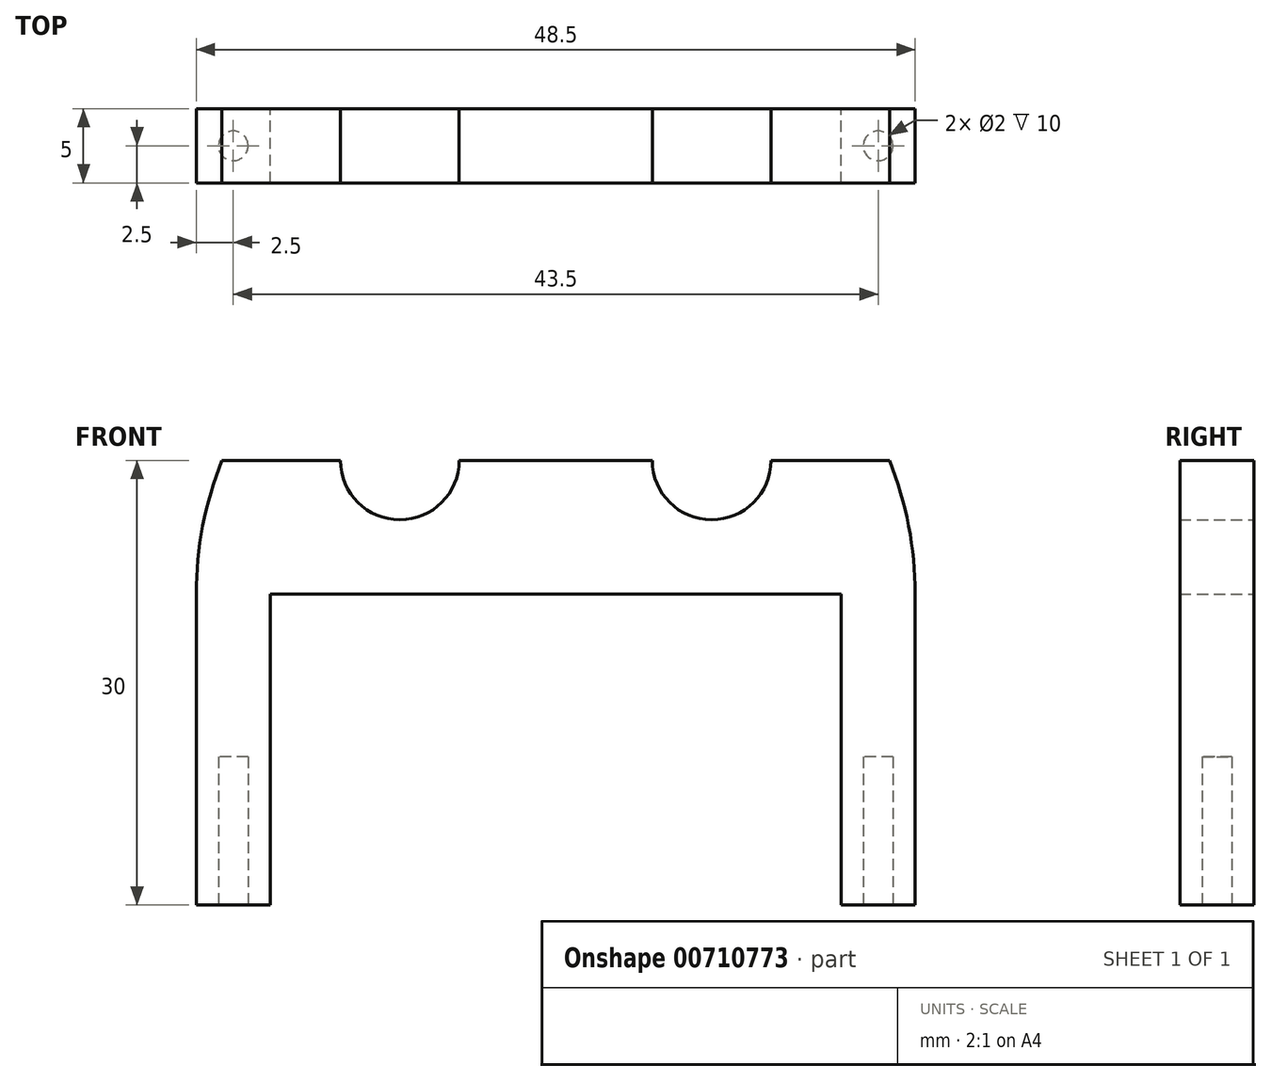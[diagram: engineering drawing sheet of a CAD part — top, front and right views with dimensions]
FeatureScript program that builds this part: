
annotation { "Feature Type Name" : "Feature", "Feature Type Description" : "" }
export const myFeature = defineFeature(function(context is Context, id is Id, definition is map)
    precondition{}
    {
        {
            var Q0;
            Q0=qCreatedBy(makeId("Front.planeOp"),FACE);
            var sketch = newSketch(context, id + "F0", { "sketchPlane" : qUnion([Q0])});
            skLineSegment(sketch, "E0", {"start": v(-24.25, 0) * mm, "end": v(-19.25, 0) * mm});
            skLineSegment(sketch, "E1", {"start": v(19.25, 0) * mm, "end": v(24.25, 0) * mm});
            skLineSegment(sketch, "E2", {"start": v(-24.25, 0) * mm, "end": v(-24.25, 21) * mm});
            skLineSegment(sketch, "E3", {"start": v(-19.25, 0) * mm, "end": v(-19.25, 21) * mm});
            skLineSegment(sketch, "E4", {"start": v(19.25, 0) * mm, "end": v(19.25, 21) * mm});
            skLineSegment(sketch, "E5", {"start": v(24.25, 0) * mm, "end": v(24.25, 21) * mm});
            skArc(sketch, "E6", {"start": v(24.25, 21) * mm, "mid": v(0, 45.25) * mm, "end": v(-24.25, 21) * mm});
            skLineSegment(sketch, "E7", {"start": v(-22.52, 30) * mm, "end": v(22.52, 30) * mm});
            skCircle(sketch, "E8", {"center": v(-10.52, 30) * mm, "radius": 4 * mm});
            skCircle(sketch, "E9", {"center": v(10.52, 30) * mm, "radius": 4 * mm});
            skLineSegment(sketch, "E10", {"start": v(0, 45.25) * mm, "end": v(0, 21) * mm});
            skCircle(sketch, "E11", {"center": v(0, 33.12) * mm, "radius": 1.75 * mm});
            skLineSegment(sketch, "E12", {"start": v(-19.25, 21) * mm, "end": v(19.25, 21) * mm});
            skSolve(sketch);
        }
        {
            var Q0;
            {var subQ1=sQuery(id+"F0.wireOp",EDGE,"E7");var subQ6=sQuery(id+"F0.wireOp",EDGE,"E6");var subQ7=makeQuery(id+"F0.imprint","INTERSECT",VERTEX,{"disambiguationData":[OD(0.0)],"derivedFrom":[subQ6,subQ1]});Q0=makeQuery(id+"F0.imprint","IMPRINT",FACE,{"disambiguationData":[TD([[makeQuery(id+"F0.imprint","IMPRINT",EDGE,{"disambiguationData":[TD([[subQ7,1.0]])],"derivedFrom":subQ6}),1.0]])]});}
            var Q1;
            {var subQ0=sQuery(id+"F0.wireOp",EDGE,"E7");var subQ1=sQuery(id+"F0.wireOp",EDGE,"E6");var subQ2=makeQuery(id+"F0.imprint","INTERSECT",VERTEX,{"disambiguationData":[OD(1.0)],"derivedFrom":[subQ1,subQ0]});Q1=makeQuery(id+"F0.imprint","IMPRINT",FACE,{"disambiguationData":[TD([[makeQuery(id+"F0.imprint","IMPRINT",EDGE,{"disambiguationData":[TD([[subQ2,-1.0]])],"derivedFrom":subQ1}),1.0]])]});}
            var Q2;
            Q2=makeQuery(id+"F0.imprint","IMPRINT",FACE,{"disambiguationData":[TD([[makeQuery(id+"F0.imprint","IMPRINT",EDGE,{"derivedFrom":sQuery(id+"F0.wireOp",EDGE,"E1")}),1.0]])]});
            var Q3;
            Q3=makeQuery(id+"F0.imprint","IMPRINT",FACE,{"disambiguationData":[TD([[makeQuery(id+"F0.imprint","IMPRINT",EDGE,{"derivedFrom":sQuery(id+"F0.wireOp",EDGE,"E0")}),1.0]])]});
            extrude(context, id + "F1", {"entities" : qUnion([Q0, Q1, Q2, Q3]), "depth" : 5 * mm, "offsetDistance" : 25 * mm});
        }
        {
            var Q0;
            Q0=qCreatedBy(makeId("Top.planeOp"),FACE);
            var sketch = newSketch(context, id + "F2", { "sketchPlane" : qUnion([Q0])});
            skCircle(sketch, "E13", {"center": v(-21.75, -2.5) * mm, "radius": 1 * mm});
            skCircle(sketch, "E14", {"center": v(21.75, -2.5) * mm, "radius": 1 * mm});
            skSolve(sketch);
        }
        {
            var Q0;
            Q0=makeQuery(id+"F2.imprint","IMPRINT",FACE,{"disambiguationData":[TD([[makeQuery(id+"F2.imprint","IMPRINT",EDGE,{"derivedFrom":sQuery(id+"F2.wireOp",EDGE,"E14")}),1.0]])]});
            var Q1;
            Q1=makeQuery(id+"F2.imprint","IMPRINT",FACE,{"disambiguationData":[TD([[makeQuery(id+"F2.imprint","IMPRINT",EDGE,{"derivedFrom":sQuery(id+"F2.wireOp",EDGE,"E13")}),1.0]])]});
            extrude(context, id + "F3", {"entities" : qUnion([Q0, Q1]), "operationType" : NewBodyOperationType.REMOVE, "depth" : 10 * mm, "offsetDistance" : 25 * mm});
        }
    });
